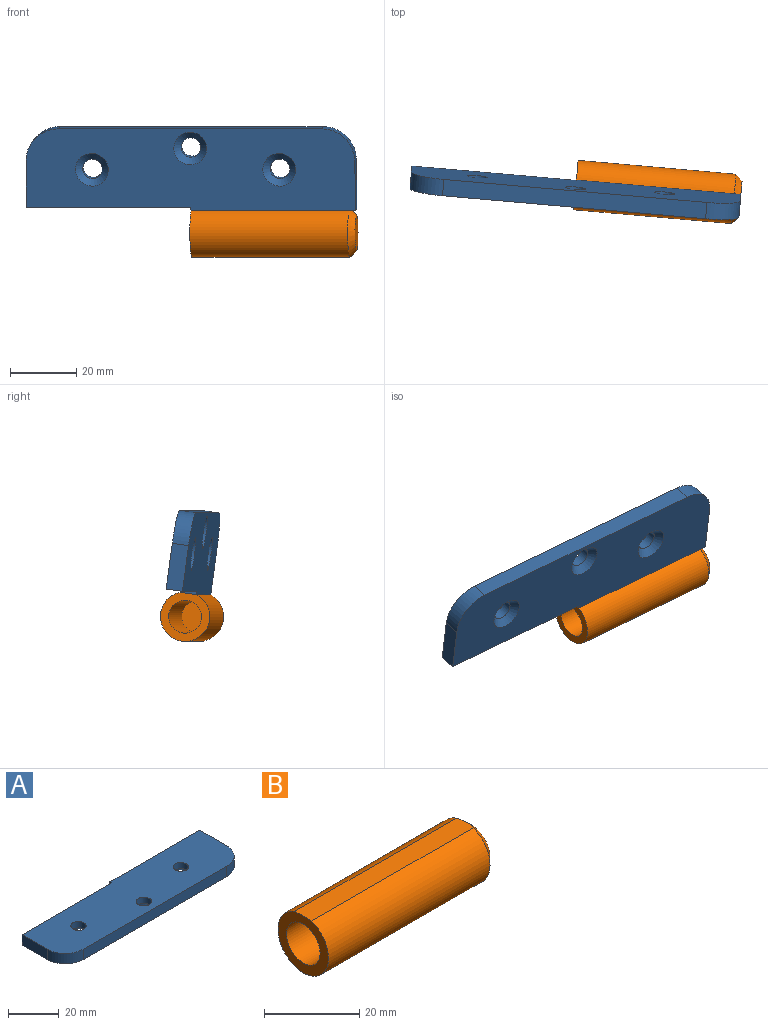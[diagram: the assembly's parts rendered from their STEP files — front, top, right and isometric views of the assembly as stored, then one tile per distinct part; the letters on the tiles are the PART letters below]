
ASSEMBLY  parts=2 mates=1
PART A: 16 faces, bbox 100x25x5 mm
  f0: plane 80x5mm, normal (0,-1,0), area 400mm2, adj f1,f7,f8,f9
  f1: cylinder r=10mm len=10mm, axis (0,0,1), area 78.5mm2, adj f0,f2,f8,f9
  f2: plane 15x5mm, normal (1,0,0), area 75mm2, adj f1,f3,f8,f9
  f3: plane 50x5mm, normal (0,1,0), area 250mm2, adj f2,f4,f8,f9
  f4: plane 5x1mm, normal (-1,0,0), area 5mm2, adj f3,f5,f8,f9
  f5: plane 50x5mm, normal (0,1,0), area 250mm2, adj f4,f6,f8,f9
  f6: plane 14x5mm, normal (-1,0,0), area 70mm2, adj f5,f7,f8,f9
  f7: cylinder r=10mm len=10mm, axis (0,0,1), area 78.5mm2, adj f0,f6,f8,f9
  f8: plane 100x25mm, normal (0,0,-1), area 2171.5mm2, adj f0,f1,f2,f3,f4,f5,f6,f7
  f9: plane 100x25mm, normal (0,0,1), area 2322.3mm2, adj f0,f1,f2,f3,f4,f5,f6,f7
  f10: cylinder r=3mm len=6mm, axis (0,0,1), area 56.5mm2, adj f9,f15
  f11: cylinder r=3mm len=6mm, axis (0,0,1), area 56.5mm2, adj f9,f13
  f12: cylinder r=3mm len=6mm, axis (0,0,1), area 56.5mm2, adj f9,f14
  f13: cone r=5mm half-angle=45deg, axis (0,0,-1), area 71.1mm2, adj f8,f11
  f14: cone r=5mm half-angle=45deg, axis (0,0,-1), area 71.1mm2, adj f8,f12
  f15: cone r=5mm half-angle=45deg, axis (0,0,-1), area 71.1mm2, adj f8,f10
PART B: 7 faces, bbox 50x15x15 mm
  f0: cylinder r=7.5mm len=48mm, axis (-1,0,0), area 2017.3mm2, adj f2,f5,f6
  f1: plane 11x11mm, normal (1,0,0), area 95mm2, adj f6
  f2: plane 15x14.57mm, normal (-1,0,0), area 96.7mm2, adj f0,f3,f5
  f3: cylinder r=5mm len=45mm, axis (-1,0,0), area 1413.7mm2, adj f2,f4
  f4: plane 10x10mm, normal (-1,0,0), area 78.5mm2, adj f3
  f5: plane 48.43x5.01mm, normal (0,0,1), area 241.4mm2, adj f0,f2,f6
  f6: cone r=5.5mm half-angle=45deg, axis (-1,0,0), area 113.5mm2, adj f0,f1,f5
PLACE A rot(axis=(-1,0.04,-0.05),82.4deg) t=(-23.55,-18.5,26.58)mm
PLACE B rot(axis=(0.84,-0.04,-0.54),9.2deg) t=(-23.54,-18.35,6.85)mm
MATE fastened A.f3 <-> B.f5  axis (-0.01,-0.13,0.99) through (26.19,-23.65,13.86)mm
